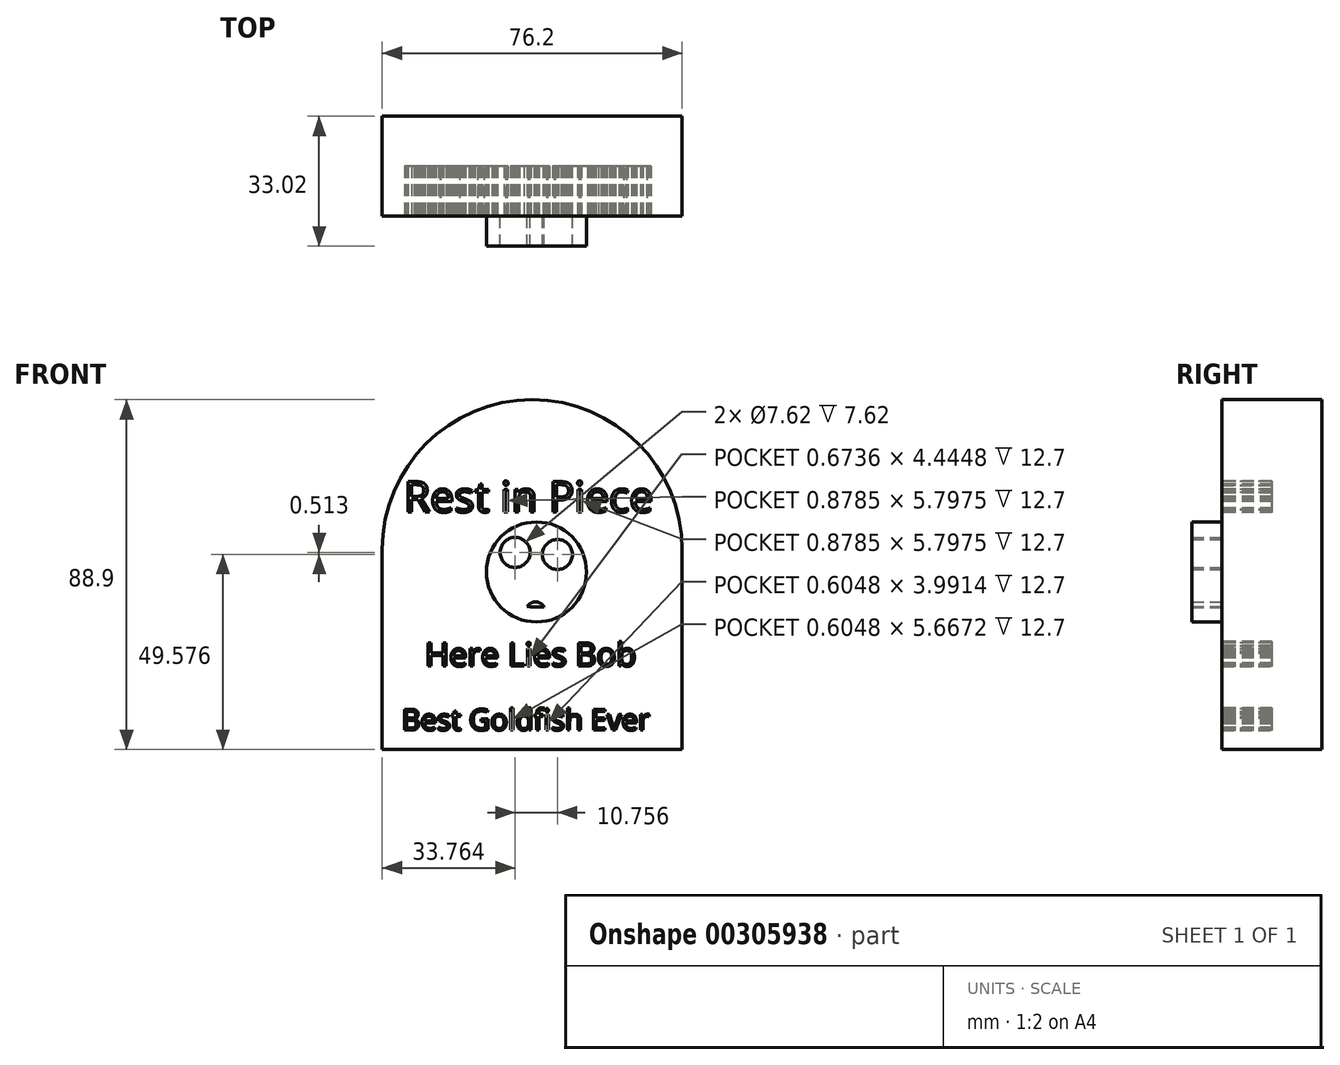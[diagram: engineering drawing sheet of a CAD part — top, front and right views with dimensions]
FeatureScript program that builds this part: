
annotation { "Feature Type Name" : "Feature", "Feature Type Description" : "" }
export const myFeature = defineFeature(function(context is Context, id is Id, definition is map)
    precondition{}
    {
        {
            var Q0;
            Q0=qCreatedBy(makeId("Front.planeOp"),FACE);
            var sketch = newSketch(context, id + "F0", { "sketchPlane" : qUnion([Q0])});
            skLineSegment(sketch, "E0", {"start": v(-44.52, -19.94) * mm, "end": v(-44.52, 30.86) * mm});
            skLineSegment(sketch, "E1", {"start": v(-44.52, -19.94) * mm, "end": v(31.68, -19.94) * mm});
            skLineSegment(sketch, "E2", {"start": v(31.68, -19.94) * mm, "end": v(31.68, 30.86) * mm});
            skArc(sketch, "E3", {"start": v(31.68, 30.86) * mm, "mid": v(-6.42, 68.96) * mm, "end": v(-44.52, 30.86) * mm});
            skSolve(sketch);
        }
        {
            var Q0;
            Q0 = qSketchRegion(id + "F0", true);
            extrude(context, id + "F1", {"entities" : qUnion([Q0]), "depth" : 25.4 * mm});
        }
        {
            var Q0;
            Q0=makeQuery(id+"F1.opExtrude","CAP_FACE",FACE,{"disambiguationData":[OSD([sQuery(id+"F0.wireOp",EDGE,"E0"),sQuery(id+"F0.wireOp",EDGE,"E1"),sQuery(id+"F0.wireOp",EDGE,"E2"),sQuery(id+"F0.wireOp",EDGE,"E3")])],"isStart":false});
            var sketch = newSketch(context, id + "F2", { "sketchPlane" : qUnion([Q0])});
            skText(sketch, "E4", { "text": "Rest in Piece", "fontName": "OpenSans-Regular.ttf"});
            skText(sketch, "E5", { "text": "Here Lies Bob", "fontName": "OpenSans-Regular.ttf"});
            skText(sketch, "E6", { "text": "Best Goldfish Ever", "fontName": "OpenSans-Regular.ttf"});
            const initialGuessF2  = {"E4": [-0.03903, 0.04041, 1, 0, 0.0078], "E5": [-0.03366, 0.00125, 1, 0, 0.00598], "E6": [-0.03964, -0.015, 1, 0, 0.00537]};
            skSetInitialGuess(sketch, initialGuessF2);
            skSolve(sketch);
        }
        {
            var Q0;
            Q0 = qSketchRegion(id + "F2", true);
            extrude(context, id + "F3", {"entities" : qUnion([Q0]), "operationType" : NewBodyOperationType.REMOVE, "oppositeDirection" : true, "depth" : 12.7 * mm});
        }
        {
            var Q0;
            {var subQ0=sQuery(id+"F0.wireOp",EDGE,"E1");var subQ1=sQuery(id+"F0.wireOp",EDGE,"E3");var subQ2=sQuery(id+"F0.wireOp",EDGE,"E0");var subQ3=sQuery(id+"F0.wireOp",EDGE,"E2");Q0=makeQuery(id+"F3.boolean.opBoolean","SPLIT",FACE,{"disambiguationData":[TD([makeQuery(id+"F1.opExtrude","SWEPT_FACE",FACE,{"disambiguationData":[OSD([subQ2])]})])],"derivedFrom":makeQuery(id+"F1.opExtrude","CAP_FACE",FACE,{"disambiguationData":[OSD([subQ2,subQ0,subQ3,subQ1])],"isStart":false})});}
            var sketch = newSketch(context, id + "F4", { "sketchPlane" : qUnion([Q0])});
            skCircle(sketch, "E7", {"center": v(-5.32, 25.19) * mm, "radius": 12.7 * mm});
            skCircle(sketch, "E8", {"center": v(-10.76, 30.15) * mm, "radius": 3.81 * mm});
            skCircle(sketch, "E9", {"center": v(0, 29.64) * mm, "radius": 3.81 * mm});
            skArc(sketch, "E10", {"start": v(-7.68, 16.45) * mm, "mid": v(-5.53, 16.24) * mm, "end": v(-3.36, 16.3) * mm});
            skArc(sketch, "E11", {"start": v(-3.36, 16.3) * mm, "mid": v(-5.48, 17.58) * mm, "end": v(-7.68, 16.45) * mm});
            skSolve(sketch);
        }
        {
            var Q0;
            Q0 = qSketchRegion(id + "F4", true);
            extrude(context, id + "F5", {"entities" : qUnion([Q0]), "operationType" : NewBodyOperationType.ADD, "depth" : 7.62 * mm});
        }
    });
